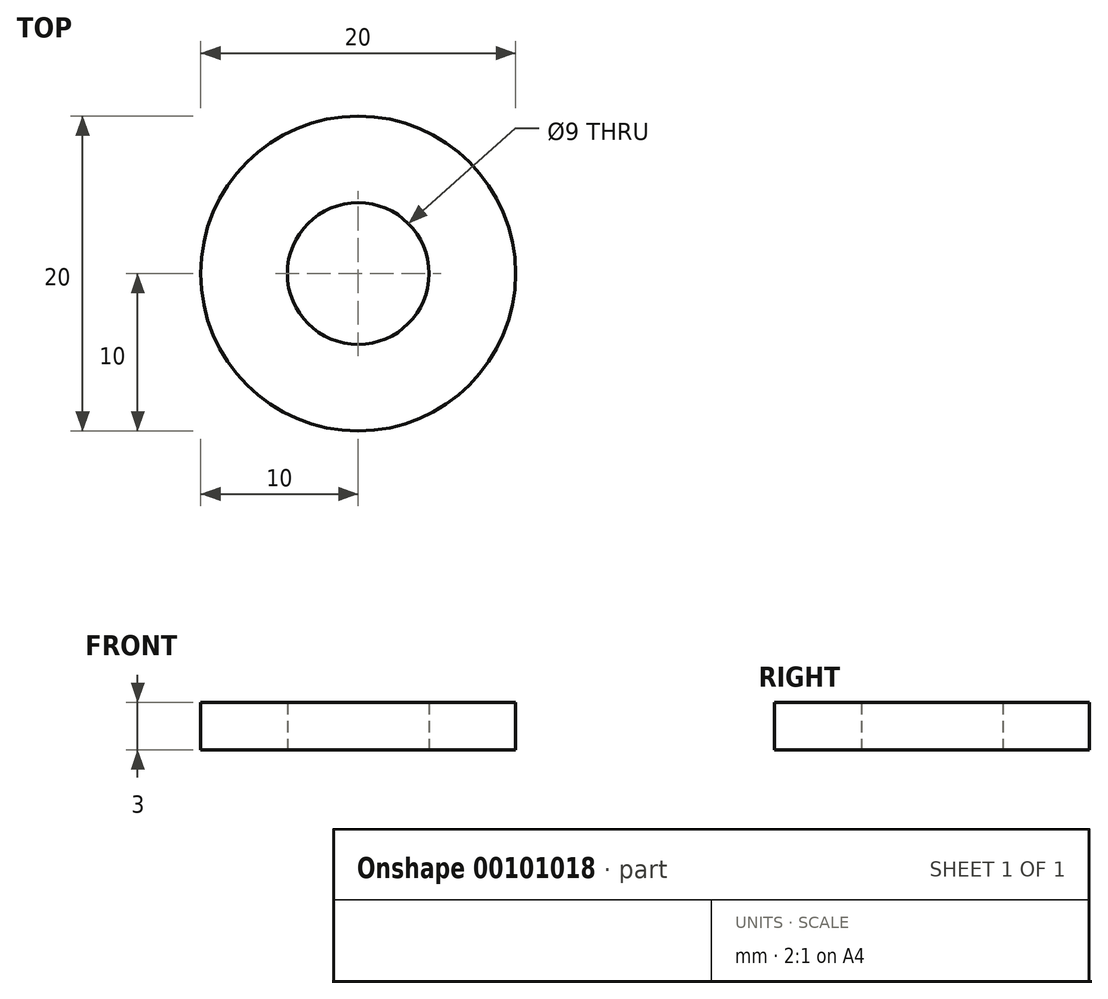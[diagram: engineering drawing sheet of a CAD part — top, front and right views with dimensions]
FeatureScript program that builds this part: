
annotation { "Feature Type Name" : "Feature", "Feature Type Description" : "" }
export const myFeature = defineFeature(function(context is Context, id is Id, definition is map)
    precondition{}
    {
        {
            var Q0;
            Q0=qCreatedBy(makeId("Top.planeOp"),FACE);
            var sketch = newSketch(context, id + "F0", { "sketchPlane" : qUnion([Q0])});
            skCircle(sketch, "E0", {"center": v(0, 0) * mm, "radius": 4.5 * mm});
            skCircle(sketch, "E1", {"center": v(0, 0) * mm, "radius": 10 * mm});
            skSolve(sketch);
        }
        {
            var Q0;
            Q0=makeQuery(id+"F0.imprint","IMPRINT",FACE,{"disambiguationData":[TD([[makeQuery(id+"F0.imprint","IMPRINT",EDGE,{"derivedFrom":sQuery(id+"F0.wireOp",EDGE,"E0")}),-1.0]])]});
            extrude(context, id + "F1", {"entities" : qUnion([Q0]), "depth" : 3 * mm});
        }
    });
